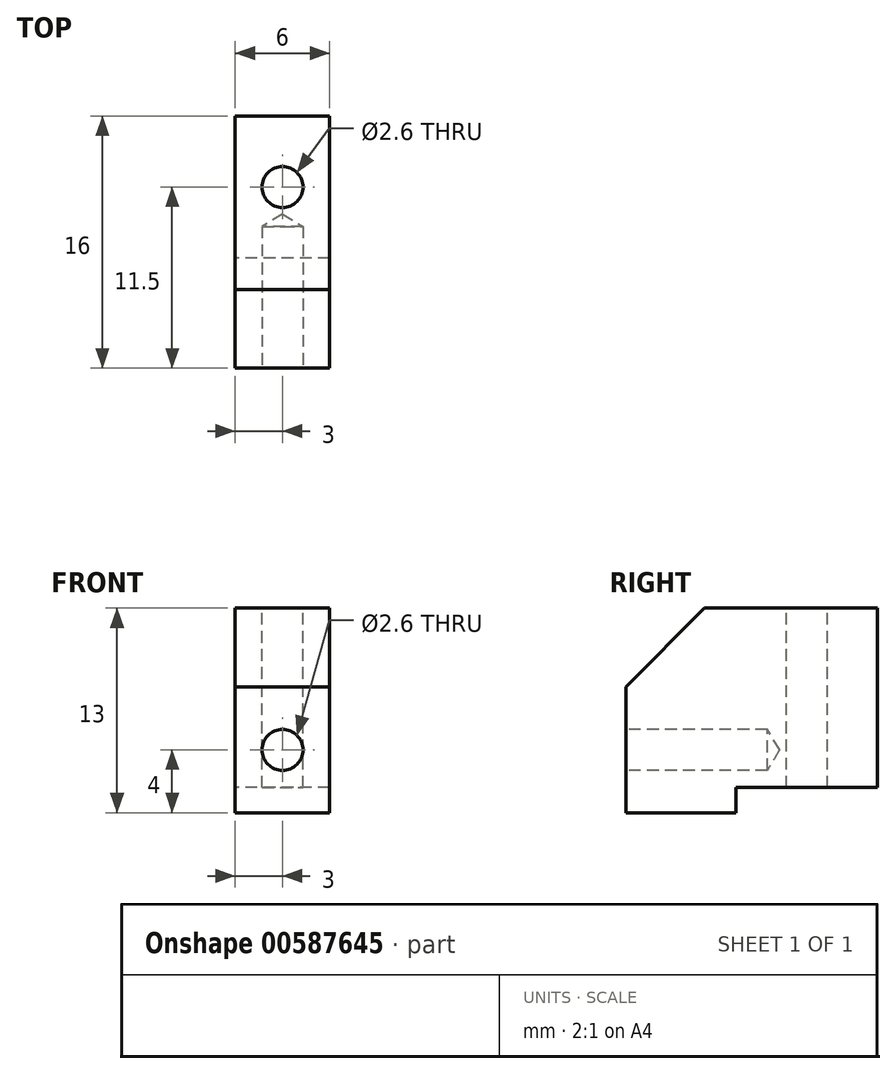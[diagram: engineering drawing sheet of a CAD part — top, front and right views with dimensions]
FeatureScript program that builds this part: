
annotation { "Feature Type Name" : "Feature", "Feature Type Description" : "" }
export const myFeature = defineFeature(function(context is Context, id is Id, definition is map)
    precondition{}
    {
        {
            var Q0;
            Q0=qCreatedBy(makeId("Right.planeOp"),FACE);
            var sketch = newSketch(context, id + "F0", { "sketchPlane" : qUnion([Q0])});
            skLineSegment(sketch, "E0", {"start": v(0, 0) * mm, "end": v(0, 8) * mm});
            skLineSegment(sketch, "E1", {"start": v(0, 8) * mm, "end": v(5, 13) * mm});
            skLineSegment(sketch, "E2", {"start": v(5, 13) * mm, "end": v(16, 13) * mm});
            skLineSegment(sketch, "E3", {"start": v(16, 13) * mm, "end": v(16, 1.6) * mm});
            skLineSegment(sketch, "E4", {"start": v(16, 1.6) * mm, "end": v(7, 1.6) * mm});
            skLineSegment(sketch, "E5", {"start": v(7, 1.6) * mm, "end": v(7, 0) * mm});
            skLineSegment(sketch, "E6", {"start": v(7, 0) * mm, "end": v(0, 0) * mm});
            skSolve(sketch);
        }
        {
            var Q0;
            Q0 = qSketchRegion(id + "F0", true);
            extrude(context, id + "F1", {"entities" : qUnion([Q0]), "depth" : 6 * mm, "offsetDistance" : 25 * mm});
        }
        {
            var Q0;
            Q0=makeQuery(id+"F1.opExtrude","SWEPT_FACE",FACE,{"disambiguationData":[OSD([sQuery(id+"F0.wireOp",EDGE,"E2")])]});
            var sketch = newSketch(context, id + "F2", { "sketchPlane" : qUnion([Q0])});
            skLineSegment(sketch, "E7", {"start": v(3, 0) * mm, "end": v(3, 16) * mm, "construction": true});
            skPoint(sketch, "E8", {"position": v(3, 11.5) * mm});
            skSolve(sketch);
        }
        {
            var Q0;
            Q0=makeQuery(id+"F1.opExtrude","SWEPT_FACE",FACE,{"disambiguationData":[OSD([sQuery(id+"F0.wireOp",EDGE,"E0")])]});
            var sketch = newSketch(context, id + "F3", { "sketchPlane" : qUnion([Q0])});
            skLineSegment(sketch, "E9", {"start": v(3, 0) * mm, "end": v(3, 8) * mm, "construction": true});
            skPoint(sketch, "E10", {"position": v(3, 4) * mm});
            skSolve(sketch);
        }
        {
            var Q0;
            Q0=sQuery(id+"F2.wireOp",VERTEX,"E8");
            var Q1;
            Q1=makeQuery(id+"F1.opExtrude","SWEPT_BODY",BODY,{"disambiguationData":[OSD([sQuery(id+"F0.wireOp",EDGE,"E0"),sQuery(id+"F0.wireOp",EDGE,"E1"),sQuery(id+"F0.wireOp",EDGE,"E2"),sQuery(id+"F0.wireOp",EDGE,"E3"),sQuery(id+"F0.wireOp",EDGE,"E4"),sQuery(id+"F0.wireOp",EDGE,"E5"),sQuery(id+"F0.wireOp",EDGE,"E6")])]});
            hole(context, id + "F4", {"style" : HoleStyle.SIMPLE, "endStyle" : HoleEndStyle.THROUGH, "holeDiameter" : 2.6 * mm, "majorDiameter" : 5 * mm, "isTappedThrough" : true, "tappedDepth" : 12 * mm, "tapClearance" : 3, "locations" : qUnion([Q0]), "scope" : qUnion([Q1])});
        }
        {
            var Q0;
            Q0=sQuery(id+"F3.wireOp",VERTEX,"E10");
            var Q1;
            Q1=makeQuery(id+"F1.opExtrude","SWEPT_BODY",BODY,{"disambiguationData":[OSD([sQuery(id+"F0.wireOp",EDGE,"E0"),sQuery(id+"F0.wireOp",EDGE,"E1"),sQuery(id+"F0.wireOp",EDGE,"E2"),sQuery(id+"F0.wireOp",EDGE,"E3"),sQuery(id+"F0.wireOp",EDGE,"E4"),sQuery(id+"F0.wireOp",EDGE,"E5"),sQuery(id+"F0.wireOp",EDGE,"E6")])]});
            hole(context, id + "F5", {"style" : HoleStyle.SIMPLE, "endStyle" : HoleEndStyle.BLIND, "holeDiameter" : 2.6 * mm, "majorDiameter" : 5 * mm, "holeDepth" : 9 * mm, "isTappedThrough" : true, "tappedDepth" : 12 * mm, "tapClearance" : 3, "locations" : qUnion([Q0]), "scope" : qUnion([Q1])});
        }
    });
